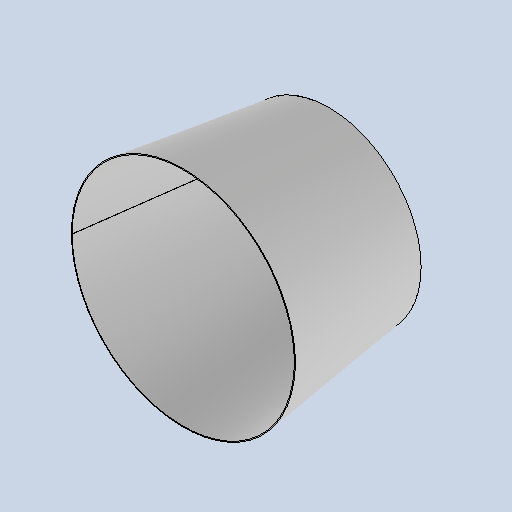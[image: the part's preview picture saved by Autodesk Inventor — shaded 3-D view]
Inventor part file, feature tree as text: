
AUTODESK INVENTOR PART (.ipt)
format: ipt  version: 2025 (Build 290162010, 162A)  size: 141,824 bytes
history: native  units: mm
features: other x2, revolve x1, sketch x1
ambient origin geometry x8: Origin, YZ Plane, XZ Plane, XY Plane, X Axis, Y Axis, Z Axis, Center Point
bodies: Solid1 (feature_tree)
feature tree (4):
  revolve  "Revolution1"  [1 undecoded]
  other  "A-Side Definition"
  sketch  "Sketch1"  dims[d0=130.0mm d3=62.8144mm d4=200.0mm d6=165.0mm d7=0.8mm]
  other  "Definition1"
note: 1 required parameter value undecoded (feature->parameter linkage not recoverable at this tier; creation-order binding heuristic only, values carry confidence <= 0.55)
